# Revit family: 50578_BEGA_Revit
name_source: partatom
category: Lighting Fixtures
revit_build: Autodesk Revit LT 2017 (Build: 20160225_1515(x64)
units: mm (PartAtom-declared; Revit-internal decimal feet)

## family parameters
Always vertical = Yes
Cut with Voids When Loaded = No
Host = Ceiling
Light Source = Yes
OmniClass Number = 23.80.70.11
OmniClass Title = Luminaries for Internal Lighting
Part Type = Normal
Room Calculation Point = No
Round Connector Dimension = Use Diameter
Shared = No

## types (2) — shared parameters
Color Filter = 16777215
Description = STUDIO LINE - recessed ceiling luminaire
Dimming Lamp Color Temperature Shift = <None>
Manufacturer = BEGA North America
Model = 50 576
Tilt Angle = 90.00°

## per-type parameters (varying)
| type | Photometric Web File |
| Semi-Recessed ceiling luminaire |  |
| STUDIO LINE - recessed ceiling luminaire | 50576.2K4_BEGA_IES.ies |

## geometry (parser evidence)
native form markers: Sweep x6
no freeform markers — native parametric forms only
